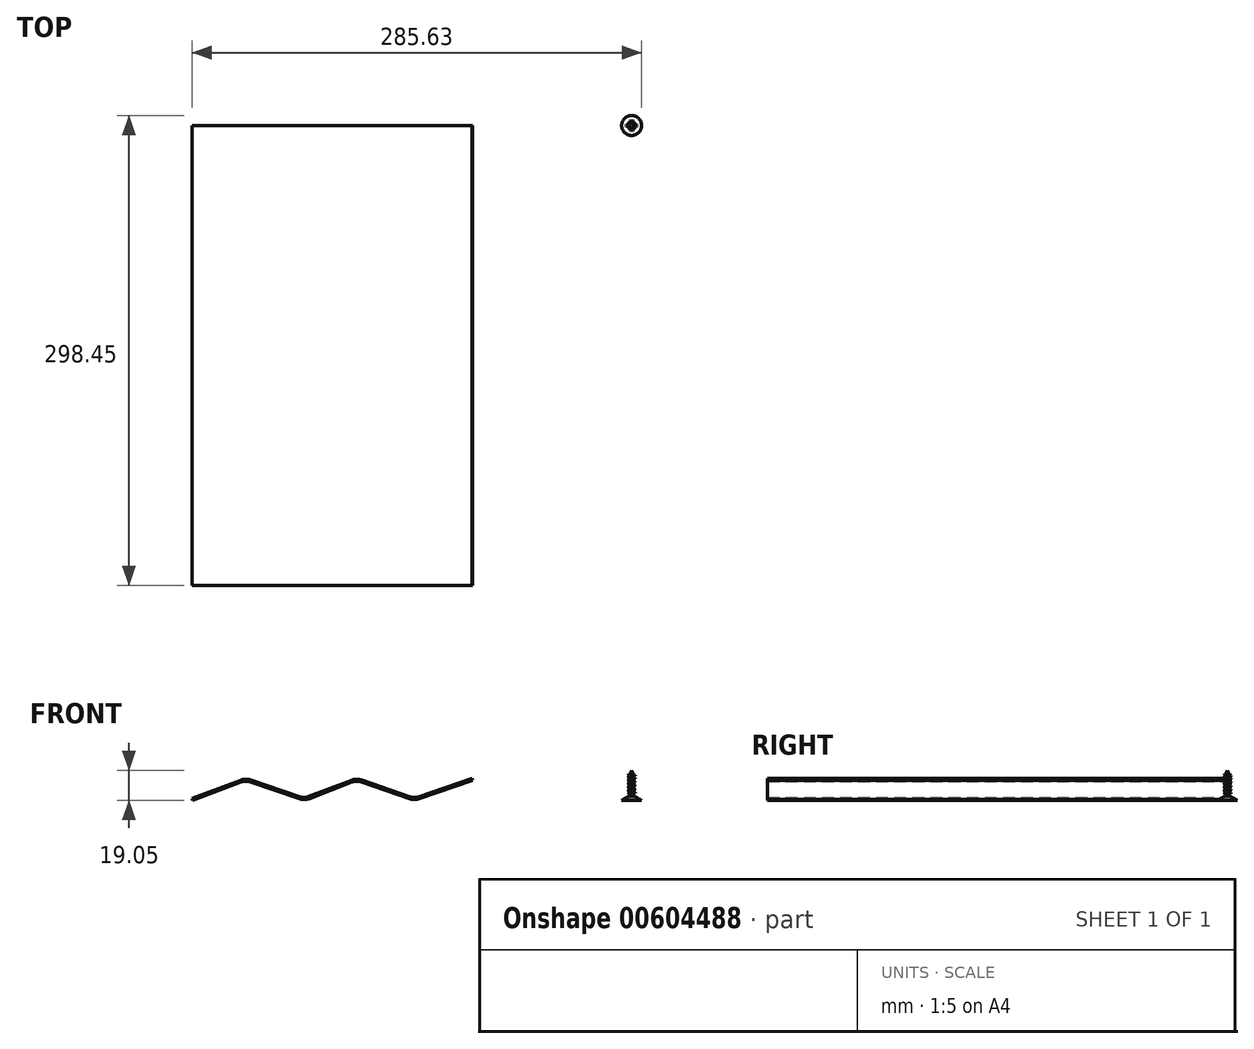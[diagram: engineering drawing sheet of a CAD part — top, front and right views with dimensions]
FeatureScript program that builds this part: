
annotation { "Feature Type Name" : "Feature", "Feature Type Description" : "" }
export const myFeature = defineFeature(function(context is Context, id is Id, definition is map)
    precondition{}
    {
        {
            var Q0;
            Q0=qCreatedBy(makeId("Front.planeOp"),FACE);
            var sketch = newSketch(context, id + "F0", { "sketchPlane" : qUnion([Q0])});
            skLineSegment(sketch, "E0", {"start": v(-278.83, 0) * mm, "end": v(-248.09, 11.64) * mm});
            skLineSegment(sketch, "E1", {"start": v(-242.43, 11.73) * mm, "end": v(-210.73, 0.97) * mm});
            skLineSegment(sketch, "E2", {"start": v(-205.03, 1.08) * mm, "end": v(-177.55, 11.6) * mm});
            skLineSegment(sketch, "E3", {"start": v(-171.8, 11.7) * mm, "end": v(-140.78, 0.95) * mm});
            skLineSegment(sketch, "E4", {"start": v(-135.32, 0.94) * mm, "end": v(-101.03, 12.7) * mm});
            skPoint(sketch, "E5.visualSharp", {"position": v(-245.28, 12.7) * mm});
            skArc(sketch, "E5.filletArc", {"start": v(-242.43, 11.73) * mm, "mid": v(-245.27, 12.18) * mm, "end": v(-248.09, 11.64) * mm});
            skPoint(sketch, "E6.visualSharp", {"position": v(-174.7, 12.7) * mm});
            skArc(sketch, "E6.filletArc", {"start": v(-171.8, 11.7) * mm, "mid": v(-174.69, 12.16) * mm, "end": v(-177.55, 11.6) * mm});
            skPoint(sketch, "E7.visualSharp", {"position": v(-138.05, 0) * mm});
            skArc(sketch, "E7.filletArc", {"start": v(-140.78, 0.95) * mm, "mid": v(-138.05, 0.48) * mm, "end": v(-135.32, 0.94) * mm});
            skPoint(sketch, "E8.visualSharp", {"position": v(-207.86, 0) * mm});
            skArc(sketch, "E8.filletArc", {"start": v(-210.73, 0.97) * mm, "mid": v(-207.87, 0.53) * mm, "end": v(-205.03, 1.08) * mm});
            skLineSegment(sketch, "E9.0", {"start": v(-135.32, 2.28) * mm, "end": v(-101.44, 13.9) * mm});
            skLineSegment(sketch, "E9.1", {"start": v(-171.4, 12.9) * mm, "end": v(-140.78, 2.29) * mm});
            skArc(sketch, "E9.2", {"start": v(-171.4, 12.9) * mm, "mid": v(-174.7, 13.43) * mm, "end": v(-178, 12.8) * mm});
            skLineSegment(sketch, "E9.3", {"start": v(-279.28, 1.19) * mm, "end": v(-248.54, 12.82) * mm});
            skArc(sketch, "E9.4", {"start": v(-242.02, 12.94) * mm, "mid": v(-245.29, 13.45) * mm, "end": v(-248.54, 12.82) * mm});
            skLineSegment(sketch, "E9.5", {"start": v(-242.02, 12.94) * mm, "end": v(-210.75, 2.32) * mm});
            skLineSegment(sketch, "E9.6", {"start": v(-205.06, 2.43) * mm, "end": v(-178, 12.8) * mm});
            skPoint(sketch, "E10.visualSharp", {"position": v(-207.89, 1.35) * mm});
            skArc(sketch, "E10.filletArc", {"start": v(-210.75, 2.32) * mm, "mid": v(-207.9, 1.88) * mm, "end": v(-205.06, 2.43) * mm});
            skPoint(sketch, "E11.visualSharp", {"position": v(-138.05, 1.34) * mm});
            skArc(sketch, "E11.filletArc", {"start": v(-140.78, 2.29) * mm, "mid": v(-138.05, 1.83) * mm, "end": v(-135.32, 2.28) * mm});
            skLineSegment(sketch, "E12", {"start": v(-101.03, 12.7) * mm, "end": v(-101.44, 13.9) * mm});
            skLineSegment(sketch, "E13", {"start": v(-278.83, 0) * mm, "end": v(-279.28, 1.19) * mm});
            skSolve(sketch);
        }
        {
            var Q0;
            Q0=qSketchRegion(id+"F0",true);
            extrude(context, id + "F1", {"entities" : qUnion([Q0]), "depth" : 292.1 * mm, "offsetDistance" : 25.4 * mm});
        }
        {
            var Q0;
            Q0=qCreatedBy(makeId("Front.planeOp"),FACE);
            var sketch = newSketch(context, id + "F2", { "sketchPlane" : qUnion([Q0])});
            skLineSegment(sketch, "E14", {"start": v(0, 0) * mm, "end": v(-6.35, 0) * mm});
            skLineSegment(sketch, "E15", {"start": v(-6.35, 0) * mm, "end": v(-1.27, 2.96) * mm});
            skLineSegment(sketch, "E16", {"start": v(-1.27, 16.26) * mm, "end": v(0, 19.05) * mm});
            skLineSegment(sketch, "E17", {"start": v(-1.27, 2.96) * mm, "end": v(-1.27, 4.5) * mm});
            skLineSegment(sketch, "E18", {"start": v(-1.27, 4.5) * mm, "end": v(-2.54, 4.95) * mm});
            skLineSegment(sketch, "E19", {"start": v(-2.54, 4.95) * mm, "end": v(-1.27, 5.37) * mm});
            skLineSegment(sketch, "E20", {"start": v(-1.27, 5.37) * mm, "end": v(-1.27, 6.75) * mm});
            skLineSegment(sketch, "E21", {"start": v(-1.27, 6.75) * mm, "end": v(-2.54, 7.2) * mm});
            skLineSegment(sketch, "E22", {"start": v(-2.54, 7.2) * mm, "end": v(-1.27, 7.63) * mm});
            skLineSegment(sketch, "E23", {"start": v(-1.27, 7.63) * mm, "end": v(-1.27, 8.98) * mm});
            skLineSegment(sketch, "E24", {"start": v(-1.27, 8.98) * mm, "end": v(-2.54, 9.5) * mm});
            skLineSegment(sketch, "E25", {"start": v(-2.54, 9.5) * mm, "end": v(-1.27, 9.92) * mm});
            skLineSegment(sketch, "E26", {"start": v(-1.27, 9.92) * mm, "end": v(-1.27, 11.34) * mm});
            skLineSegment(sketch, "E27", {"start": v(-1.27, 11.34) * mm, "end": v(-2.54, 11.76) * mm});
            skLineSegment(sketch, "E28", {"start": v(-2.54, 11.76) * mm, "end": v(-1.27, 12.18) * mm});
            skLineSegment(sketch, "E29", {"start": v(-1.27, 12.18) * mm, "end": v(-1.27, 13.64) * mm});
            skLineSegment(sketch, "E30", {"start": v(-1.27, 13.64) * mm, "end": v(-2.54, 14.1) * mm});
            skLineSegment(sketch, "E31", {"start": v(-2.54, 14.1) * mm, "end": v(-1.27, 14.52) * mm});
            skLineSegment(sketch, "E32", {"start": v(-1.27, 14.52) * mm, "end": v(-1.27, 15.38) * mm});
            skLineSegment(sketch, "E33", {"start": v(-1.27, 15.38) * mm, "end": v(-2.54, 15.76) * mm});
            skLineSegment(sketch, "E34", {"start": v(-2.54, 15.76) * mm, "end": v(-1.27, 16.26) * mm});
            skPoint(sketch, "E35", {"position": v(-1.27, 10.63) * mm});
            skLineSegment(sketch, "E36", {"start": v(-3.4, 10.63) * mm, "end": v(3.08, 10.63) * mm, "construction": true});
            skLineSegment(sketch, "E37", {"start": v(0, 19.05) * mm, "end": v(0, 0) * mm});
            skSolve(sketch);
        }
        {
            var Q0;
            Q0=makeQuery(id+"F2.imprint","IMPRINT",FACE,{"disambiguationData":[TD([[makeQuery(id+"F2.imprint","IMPRINT",EDGE,{"derivedFrom":sQuery(id+"F2.wireOp",EDGE,"E14")}),-1.0]])]});
            var Q1;
            Q1=sQuery(id+"F2.wireOp",EDGE,"E37");
            revolve(context, id + "F3", {"entities" : qUnion([Q0]), "axis" : qUnion([Q1]), "revolveType" : RevolveType.FULL});
        }
        {
            var Q0;
            Q0=makeQuery(id+"F3.opRevolve","SWEPT_FACE",FACE,{"disambiguationData":[OSD([sQuery(id+"F2.wireOp",EDGE,"E14")])]});
            var sketch = newSketch(context, id + "F4", { "sketchPlane" : qUnion([Q0])});
            skLineSegment(sketch, "E38", {"start": v(-1.04, 3.9) * mm, "end": v(-1.04, 1.01) * mm});
            skLineSegment(sketch, "E39", {"start": v(-1.04, 1.01) * mm, "end": v(-3.87, 1.01) * mm});
            skLineSegment(sketch, "E40", {"start": v(-3.87, 1.01) * mm, "end": v(-3.87, -1.01) * mm});
            skLineSegment(sketch, "E41", {"start": v(-3.87, -1.01) * mm, "end": v(-1.04, -1.01) * mm});
            skLineSegment(sketch, "E42", {"start": v(-1.04, -1.01) * mm, "end": v(-1.04, -3.9) * mm});
            skLineSegment(sketch, "E43", {"start": v(-1.04, -3.9) * mm, "end": v(1.04, -3.9) * mm});
            skLineSegment(sketch, "E44", {"start": v(1.04, -3.9) * mm, "end": v(1.04, -1.01) * mm});
            skLineSegment(sketch, "E45", {"start": v(1.04, -1.01) * mm, "end": v(3.87, -1.01) * mm});
            skLineSegment(sketch, "E46", {"start": v(3.87, -1.01) * mm, "end": v(3.87, 1.01) * mm});
            skLineSegment(sketch, "E47", {"start": v(3.87, 1.01) * mm, "end": v(1.04, 1.01) * mm});
            skLineSegment(sketch, "E48", {"start": v(1.04, 1.01) * mm, "end": v(1.04, 3.9) * mm});
            skLineSegment(sketch, "E49", {"start": v(1.04, 3.9) * mm, "end": v(-1.04, 3.9) * mm});
            skLineSegment(sketch, "E50", {"start": v(-7.36, 0) * mm, "end": v(7.8, 0) * mm, "construction": true});
            skLineSegment(sketch, "E51", {"start": v(0, 8.09) * mm, "end": v(0, -9.13) * mm, "construction": true});
            skSolve(sketch);
        }
        {
            var Q0;
            Q0=makeQuery(id+"F4.imprint","IMPRINT",FACE,{"disambiguationData":[TD([[makeQuery(id+"F4.imprint","IMPRINT",EDGE,{"derivedFrom":sQuery(id+"F4.wireOp",EDGE,"E38")}),1.0]])]});
            extrude(context, id + "F5", {"entities" : qUnion([Q0]), "operationType" : NewBodyOperationType.REMOVE, "oppositeDirection" : true, "depth" : 1.27 * mm, "offsetDistance" : 25.4 * mm});
        }
    });
